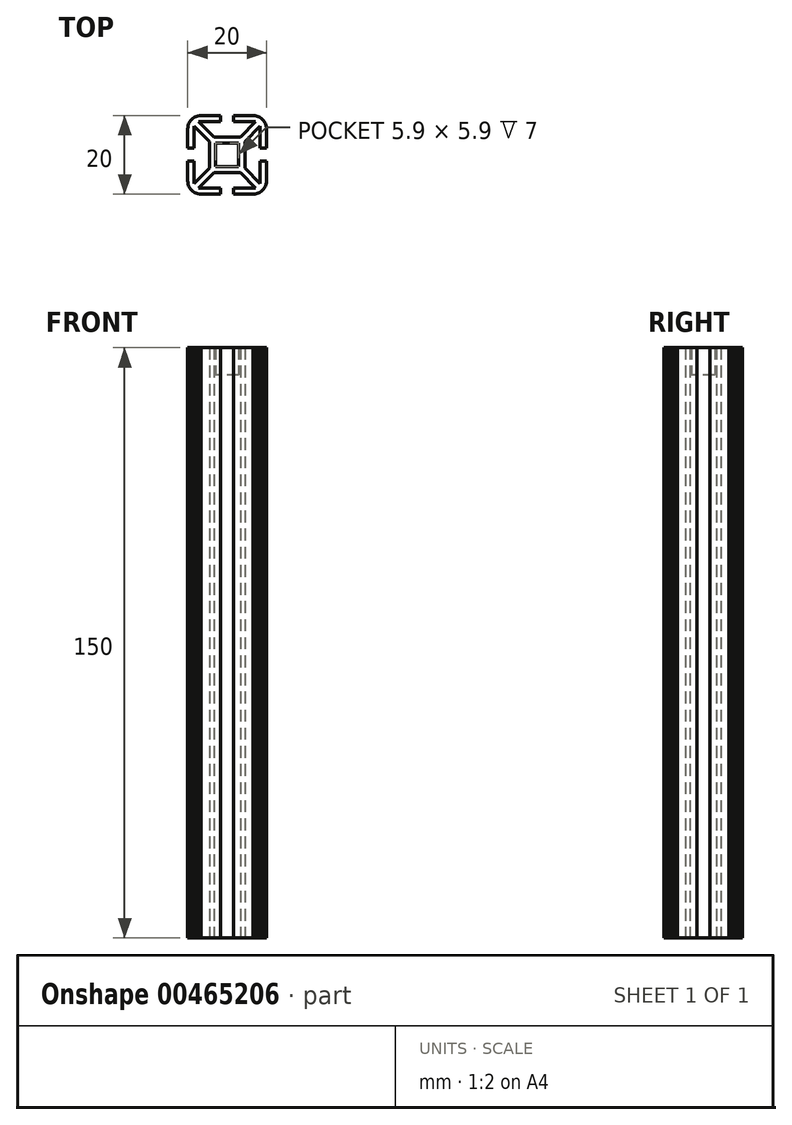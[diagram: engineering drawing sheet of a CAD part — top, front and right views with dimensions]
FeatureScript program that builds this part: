
annotation { "Feature Type Name" : "Feature", "Feature Type Description" : "" }
export const myFeature = defineFeature(function(context is Context, id is Id, definition is map)
    precondition{}
    {
        {
            var Q0;
            Q0=qCreatedBy(makeId("Top.planeOp"),FACE);
            var sketch = newSketch(context, id + "F0", { "sketchPlane" : qUnion([Q0])});
            skLineSegment(sketch, "E0", {"start": v(-9, 9) * mm, "end": v(-9.3, 8.66) * mm});
            skLineSegment(sketch, "E1", {"start": v(-9.54, 8.3) * mm, "end": v(-9.74, 7.9) * mm});
            skLineSegment(sketch, "E2", {"start": v(8.3, -9.54) * mm, "end": v(8.66, -9.3) * mm});
            skLineSegment(sketch, "E3", {"start": v(9.88, -7.47) * mm, "end": v(9.97, -7.03) * mm});
            skLineSegment(sketch, "E4", {"start": v(8.66, 9.3) * mm, "end": v(8.3, 9.54) * mm});
            skLineSegment(sketch, "E5", {"start": v(9.3, -8.66) * mm, "end": v(9.54, -8.3) * mm});
            skLineSegment(sketch, "E6", {"start": v(-8.3, 9.54) * mm, "end": v(-8.66, 9.3) * mm});
            skLineSegment(sketch, "E7", {"start": v(9.54, 8.3) * mm, "end": v(9.3, 8.66) * mm});
            skLineSegment(sketch, "E8", {"start": v(-4.5, 3.37) * mm, "end": v(-4.5, -3.37) * mm});
            skLineSegment(sketch, "E9", {"start": v(-10, -6.59) * mm, "end": v(-9.97, -7.03) * mm});
            skLineSegment(sketch, "E10", {"start": v(-10, 1.65) * mm, "end": v(-10, 6.59) * mm});
            skLineSegment(sketch, "E11", {"start": v(-10, -6.59) * mm, "end": v(-10, -1.65) * mm});
            skLineSegment(sketch, "E12", {"start": v(-9.97, -7.03) * mm, "end": v(-9.88, -7.47) * mm});
            skLineSegment(sketch, "E13", {"start": v(-9.88, -7.47) * mm, "end": v(-9.74, -7.9) * mm});
            skLineSegment(sketch, "E14", {"start": v(-9.74, -7.9) * mm, "end": v(-9.54, -8.3) * mm});
            skLineSegment(sketch, "E15", {"start": v(-9.54, -8.3) * mm, "end": v(-9.3, -8.66) * mm});
            skLineSegment(sketch, "E16", {"start": v(-9.3, -8.66) * mm, "end": v(-9, -9) * mm});
            skLineSegment(sketch, "E17", {"start": v(-9, -9) * mm, "end": v(-8.66, -9.3) * mm});
            skLineSegment(sketch, "E18", {"start": v(-8.66, -9.3) * mm, "end": v(-8.3, -9.54) * mm});
            skLineSegment(sketch, "E19", {"start": v(-8.3, -9.54) * mm, "end": v(-7.9, -9.74) * mm});
            skLineSegment(sketch, "E20", {"start": v(-7.9, -9.74) * mm, "end": v(-7.47, -9.88) * mm});
            skLineSegment(sketch, "E21", {"start": v(-7.47, -9.88) * mm, "end": v(-7.03, -9.97) * mm});
            skLineSegment(sketch, "E22", {"start": v(-7.03, -9.97) * mm, "end": v(-6.59, -10) * mm});
            skLineSegment(sketch, "E23", {"start": v(-1.65, -10) * mm, "end": v(-6.59, -10) * mm});
            skLineSegment(sketch, "E24", {"start": v(-3.37, -4.5) * mm, "end": v(3.37, -4.5) * mm});
            skLineSegment(sketch, "E25", {"start": v(6.59, -10) * mm, "end": v(1.65, -10) * mm});
            skLineSegment(sketch, "E26", {"start": v(6.59, -10) * mm, "end": v(7.03, -9.97) * mm});
            skLineSegment(sketch, "E27", {"start": v(7.03, -9.97) * mm, "end": v(7.47, -9.88) * mm});
            skLineSegment(sketch, "E28", {"start": v(7.47, -9.88) * mm, "end": v(7.9, -9.74) * mm});
            skLineSegment(sketch, "E29", {"start": v(7.9, -9.74) * mm, "end": v(8.3, -9.54) * mm});
            skLineSegment(sketch, "E30", {"start": v(8.66, -9.3) * mm, "end": v(9, -9) * mm});
            skLineSegment(sketch, "E31", {"start": v(9, -9) * mm, "end": v(9.3, -8.66) * mm});
            skLineSegment(sketch, "E32", {"start": v(9.54, -8.3) * mm, "end": v(9.74, -7.9) * mm});
            skLineSegment(sketch, "E33", {"start": v(9.74, -7.9) * mm, "end": v(9.88, -7.47) * mm});
            skLineSegment(sketch, "E34", {"start": v(9.97, -7.03) * mm, "end": v(10, -6.59) * mm});
            skLineSegment(sketch, "E35", {"start": v(10, -1.65) * mm, "end": v(10, -6.59) * mm});
            skLineSegment(sketch, "E36", {"start": v(4.5, -3.37) * mm, "end": v(4.5, 3.37) * mm});
            skLineSegment(sketch, "E37", {"start": v(10, 6.59) * mm, "end": v(10, 1.65) * mm});
            skLineSegment(sketch, "E38", {"start": v(10, 6.59) * mm, "end": v(9.97, 7.03) * mm});
            skLineSegment(sketch, "E39", {"start": v(9.97, 7.03) * mm, "end": v(9.88, 7.47) * mm});
            skLineSegment(sketch, "E40", {"start": v(9.88, 7.47) * mm, "end": v(9.74, 7.9) * mm});
            skLineSegment(sketch, "E41", {"start": v(9.74, 7.9) * mm, "end": v(9.54, 8.3) * mm});
            skLineSegment(sketch, "E42", {"start": v(9.3, 8.66) * mm, "end": v(9, 9) * mm});
            skLineSegment(sketch, "E43", {"start": v(9, 9) * mm, "end": v(8.66, 9.3) * mm});
            skLineSegment(sketch, "E44", {"start": v(8.3, 9.54) * mm, "end": v(7.9, 9.74) * mm});
            skLineSegment(sketch, "E45", {"start": v(7.9, 9.74) * mm, "end": v(7.47, 9.88) * mm});
            skLineSegment(sketch, "E46", {"start": v(7.47, 9.88) * mm, "end": v(7.03, 9.97) * mm});
            skLineSegment(sketch, "E47", {"start": v(7.03, 9.97) * mm, "end": v(6.59, 10) * mm});
            skLineSegment(sketch, "E48", {"start": v(1.65, 10) * mm, "end": v(6.59, 10) * mm});
            skLineSegment(sketch, "E49", {"start": v(3.37, 4.5) * mm, "end": v(-3.37, 4.5) * mm});
            skLineSegment(sketch, "E50", {"start": v(-6.59, 10) * mm, "end": v(-7.03, 9.97) * mm});
            skLineSegment(sketch, "E51", {"start": v(-7.03, 9.97) * mm, "end": v(-7.47, 9.88) * mm});
            skLineSegment(sketch, "E52", {"start": v(-7.47, 9.88) * mm, "end": v(-7.9, 9.74) * mm});
            skLineSegment(sketch, "E53", {"start": v(-7.9, 9.74) * mm, "end": v(-8.3, 9.54) * mm});
            skLineSegment(sketch, "E54", {"start": v(-8.66, 9.3) * mm, "end": v(-9, 9) * mm});
            skLineSegment(sketch, "E55", {"start": v(-9.3, 8.66) * mm, "end": v(-9.54, 8.3) * mm});
            skLineSegment(sketch, "E56", {"start": v(-9.74, 7.9) * mm, "end": v(-9.88, 7.47) * mm});
            skLineSegment(sketch, "E57", {"start": v(-9.88, 7.47) * mm, "end": v(-9.97, 7.03) * mm});
            skLineSegment(sketch, "E58", {"start": v(-9.97, 7.03) * mm, "end": v(-10, 6.59) * mm});
            skLineSegment(sketch, "E59", {"start": v(-4.5, -3.37) * mm, "end": v(-8.4, -7.27) * mm});
            skLineSegment(sketch, "E60", {"start": v(-8.4, -1.65) * mm, "end": v(-10, -1.65) * mm});
            skLineSegment(sketch, "E61", {"start": v(-8.4, -7.27) * mm, "end": v(-8.4, -1.65) * mm});
            skLineSegment(sketch, "E62", {"start": v(-3.37, -4.5) * mm, "end": v(-7.27, -8.4) * mm});
            skLineSegment(sketch, "E63", {"start": v(-1.65, -8.4) * mm, "end": v(-1.65, -10) * mm});
            skLineSegment(sketch, "E64", {"start": v(-7.27, -8.4) * mm, "end": v(-1.65, -8.4) * mm});
            skLineSegment(sketch, "E65", {"start": v(-4.5, 3.37) * mm, "end": v(-8.4, 7.27) * mm});
            skLineSegment(sketch, "E66", {"start": v(-8.4, 1.65) * mm, "end": v(-10, 1.65) * mm});
            skLineSegment(sketch, "E67", {"start": v(-8.4, 7.27) * mm, "end": v(-8.4, 1.65) * mm});
            skLineSegment(sketch, "E68", {"start": v(-3.37, 4.5) * mm, "end": v(-7.27, 8.4) * mm});
            skLineSegment(sketch, "E69", {"start": v(-1.65, 8.4) * mm, "end": v(-1.65, 10) * mm});
            skLineSegment(sketch, "E70", {"start": v(-7.27, 8.4) * mm, "end": v(-1.65, 8.4) * mm});
            skLineSegment(sketch, "E71", {"start": v(3.37, 4.5) * mm, "end": v(7.27, 8.4) * mm});
            skLineSegment(sketch, "E72", {"start": v(1.65, 8.4) * mm, "end": v(1.65, 10) * mm});
            skLineSegment(sketch, "E73", {"start": v(7.27, 8.4) * mm, "end": v(1.65, 8.4) * mm});
            skLineSegment(sketch, "E74", {"start": v(4.5, 3.37) * mm, "end": v(8.4, 7.27) * mm});
            skLineSegment(sketch, "E75", {"start": v(8.4, 1.65) * mm, "end": v(10, 1.65) * mm});
            skLineSegment(sketch, "E76", {"start": v(8.4, 7.27) * mm, "end": v(8.4, 1.65) * mm});
            skLineSegment(sketch, "E77", {"start": v(4.5, -3.37) * mm, "end": v(8.4, -7.27) * mm});
            skLineSegment(sketch, "E78", {"start": v(8.4, -1.65) * mm, "end": v(10, -1.65) * mm});
            skLineSegment(sketch, "E79", {"start": v(8.4, -7.27) * mm, "end": v(8.4, -1.65) * mm});
            skLineSegment(sketch, "E80", {"start": v(3.37, -4.5) * mm, "end": v(7.27, -8.4) * mm});
            skLineSegment(sketch, "E81", {"start": v(1.65, -8.4) * mm, "end": v(1.65, -10) * mm});
            skLineSegment(sketch, "E82", {"start": v(7.27, -8.4) * mm, "end": v(1.65, -8.4) * mm});
            skLineSegment(sketch, "E83", {"start": v(-1.65, 10) * mm, "end": v(-6.59, 10) * mm});
            skSolve(sketch);
        }
        {
            var Q0;
            Q0=qSketchRegion(id+"F0",true);
            extrude(context, id + "F1", {"entities" : qUnion([Q0]), "depth" : 150 * mm});
        }
        {
            var Q0;
            Q0=qCreatedBy(makeId("Top.planeOp"),FACE);
            var sketch = newSketch(context, id + "F2", { "sketchPlane" : qUnion([Q0])});
            skLineSegment(sketch, "E84.bottom", {"start": v(2.95, 2.95) * mm, "end": v(-2.95, 2.95) * mm});
            skLineSegment(sketch, "E84.top", {"start": v(2.95, -2.95) * mm, "end": v(-2.95, -2.95) * mm});
            skLineSegment(sketch, "E84.left", {"start": v(2.95, 2.95) * mm, "end": v(2.95, -2.95) * mm});
            skLineSegment(sketch, "E84.right", {"start": v(-2.95, 2.95) * mm, "end": v(-2.95, -2.95) * mm});
            skPoint(sketch, "E84.middle", {"position": v(0, 0) * mm});
            skSolve(sketch);
        }
        {
            var Q0;
            Q0=qSketchRegion(id+"F2",true);
            extrude(context, id + "F3", {"entities" : qUnion([Q0]), "operationType" : NewBodyOperationType.REMOVE, "depth" : 157 * mm, "hasSecondDirection" : true, "secondDirectionOppositeDirection" : false, "secondDirectionDepth" : 143 * mm});
        }
    });
